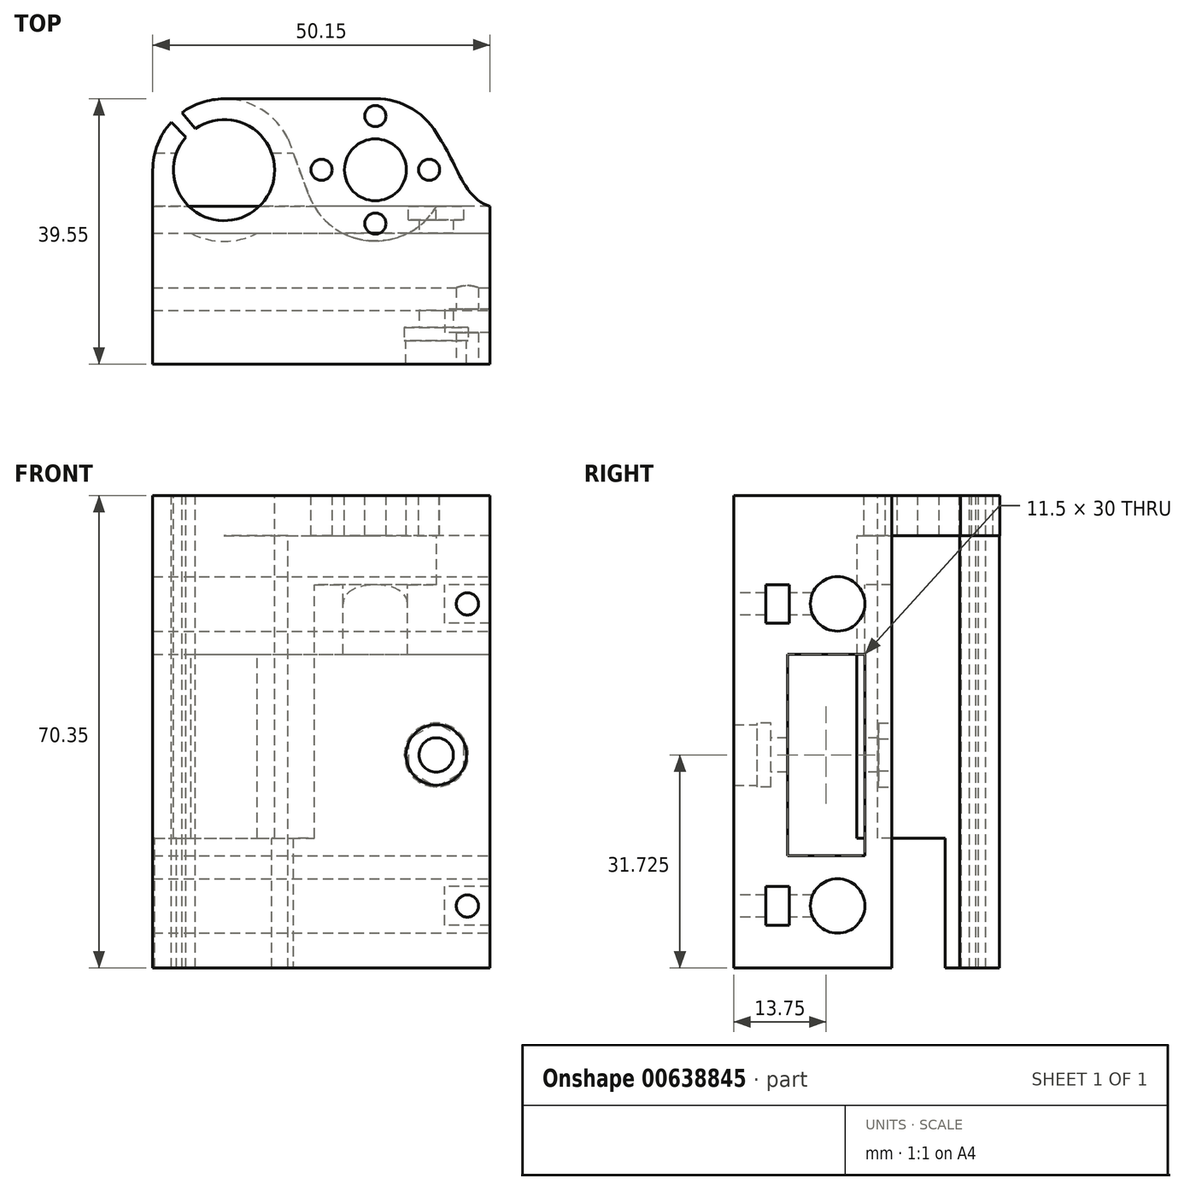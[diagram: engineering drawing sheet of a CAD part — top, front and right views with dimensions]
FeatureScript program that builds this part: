
annotation { "Feature Type Name" : "Feature", "Feature Type Description" : "" }
export const myFeature = defineFeature(function(context is Context, id is Id, definition is map)
    precondition{}
    {
        {
            var Q0;
            Q0=qCreatedBy(makeId("Top.planeOp"),FACE);
            var sketch = newSketch(context, id + "F0", { "sketchPlane" : qUnion([Q0])});
            skArc(sketch, "E0", {"start": v(-30.36, 19.22) * mm, "mid": v(-32.39, 15.91) * mm, "end": v(-33.1, 12.1) * mm});
            skCircle(sketch, "E1", {"center": v(0, 12.15) * mm, "radius": 10.6 * mm});
            skLineSegment(sketch, "E2", {"start": v(-33.1, 12.1) * mm, "end": v(-33.1, -13.3) * mm});
            skLineSegment(sketch, "E3", {"start": v(-33.1, -13.3) * mm, "end": v(17.05, -13.3) * mm});
            skLineSegment(sketch, "E4", {"start": v(17.05, -13.3) * mm, "end": v(17.05, 6.7) * mm});
            skArc(sketch, "E5", {"start": v(-28.18, 17.02) * mm, "mid": v(-17.48, 6.5) * mm, "end": v(-26.77, 18.29) * mm});
            skCircle(sketch, "E6", {"center": v(0, 12.15) * mm, "radius": 4.6 * mm});
            skLineSegment(sketch, "E7", {"start": v(-26.77, 18.29) * mm, "end": v(-28.78, 20.64) * mm});
            skLineSegment(sketch, "E8", {"start": v(-30.36, 19.22) * mm, "end": v(-28.18, 17.02) * mm});
            skArc(sketch, "E9.trimOffspring", {"start": v(-13, 16.8) * mm, "mid": v(-20, 22.4) * mm, "end": v(-28.78, 20.64) * mm});
            skCircle(sketch, "E10", {"center": v(0, 20.15) * mm, "radius": 1.57 * mm});
            skCircle(sketch, "E11", {"center": v(0, 4.15) * mm, "radius": 1.57 * mm});
            skCircle(sketch, "E12", {"center": v(8, 12.15) * mm, "radius": 1.57 * mm});
            skCircle(sketch, "E13", {"center": v(-8, 12.15) * mm, "radius": 1.57 * mm});
            skLineSegment(sketch, "E14", {"start": v(-13, 16.8) * mm, "end": v(-9.95, 8.5) * mm});
            skLineSegment(sketch, "E15", {"start": v(17.05, 6.7) * mm, "end": v(9.1, 6.7) * mm});
            skLineSegment(sketch, "E16", {"start": v(-22.52, 22.7) * mm, "end": v(0, 22.75) * mm});
            skFitSpline(sketch, "E17", {"points": [v(17.05, 6.7) * mm, v(9.47, 16.92) * mm], "startDerivative": vector(-12.18, 3.65) * mm, "endDerivative": vector(-7.6, 10.22) * mm});
            skCircle(sketch, "E18", {"center": v(-22.5, 12.1) * mm, "radius": 10.6 * mm});
            skSolve(sketch);
        }
        {
            var Q0;
            Q0=makeQuery(id+"F0.imprint","IMPRINT",FACE,{"disambiguationData":[TD([[makeQuery(id+"F0.imprint","IMPRINT",EDGE,{"derivedFrom":sQuery(id+"F0.wireOp",EDGE,"E0")}),1.0]])]});
            var Q1;
            {var subQ6=sQuery(id+"F0.wireOp",EDGE,"E2");Q1=makeQuery(id+"F0.imprint","IMPRINT",FACE,{"disambiguationData":[TD([[makeQuery(id+"F0.imprint","IMPRINT",EDGE,{"derivedFrom":subQ6}),1.0]])]});}
            extrude(context, id + "F1", {"entities" : qUnion([Q0, Q1]), "depth" : -70.35 * mm, "offsetDistance" : 25 * mm});
        }
        {
            var Q0;
            Q0=makeQuery(id+"F0.imprint","IMPRINT",FACE,{"disambiguationData":[TD([[makeQuery(id+"F0.imprint","IMPRINT",EDGE,{"derivedFrom":sQuery(id+"F0.wireOp",EDGE,"E6")}),-1.0]])]});
            var Q1;
            Q1 = qSketchRegion(id + "F3", true);
            var Q2;
            {var subQ0=sQuery(id+"F0.wireOp",EDGE,"E15");Q2=makeQuery(id+"F0.imprint","IMPRINT",FACE,{"disambiguationData":[TD([[makeQuery(id+"F0.imprint","IMPRINT",EDGE,{"derivedFrom":subQ0}),-1.0]])]});}
            var Q3;
            {var subQ0=sQuery(id+"F0.wireOp",EDGE,"E14");Q3=makeQuery(id+"F0.imprint","IMPRINT",FACE,{"disambiguationData":[TD([[makeQuery(id+"F0.imprint","IMPRINT",EDGE,{"derivedFrom":subQ0}),1.0]])]});}
            var Q4;
            {var subQ4=sQuery(id+"F0.wireOp",EDGE,"E16");Q4=makeQuery(id+"F0.imprint","IMPRINT",FACE,{"disambiguationData":[TD([[makeQuery(id+"F0.imprint","IMPRINT",EDGE,{"derivedFrom":subQ4}),-1.0]])]});}
            extrude(context, id + "F2", {"entities" : qUnion([Q0, Q1, Q2, Q3, Q4]), "operationType" : NewBodyOperationType.ADD, "depth" : -6 * mm, "offsetDistance" : 25 * mm});
        }
        {
            var Q0;
            Q0=qCreatedBy(makeId("Right.planeOp"),FACE);
            var sketch = newSketch(context, id + "F3", { "sketchPlane" : qUnion([Q0])});
            skCircle(sketch, "E19", {"center": v(-1.35, -16.15) * mm, "radius": 4.05 * mm});
            skCircle(sketch, "E20", {"center": v(-1.35, -61.1) * mm, "radius": 4.05 * mm});
            skLineSegment(sketch, "E21.bottom", {"start": v(2.7, -53.62) * mm, "end": v(-8.8, -53.62) * mm});
            skLineSegment(sketch, "E21.top", {"start": v(2.7, -23.62) * mm, "end": v(-8.8, -23.62) * mm});
            skLineSegment(sketch, "E21.left", {"start": v(2.7, -53.62) * mm, "end": v(2.7, -23.62) * mm});
            skLineSegment(sketch, "E21.right", {"start": v(-8.8, -53.62) * mm, "end": v(-8.8, -23.62) * mm});
            skPoint(sketch, "E21.middle", {"position": v(-3.05, -38.62) * mm});
            skSolve(sketch);
        }
        {
            var Q0;
            Q0=makeQuery(id+"F3.imprint","IMPRINT",FACE,{"disambiguationData":[TD([[makeQuery(id+"F3.imprint","IMPRINT",EDGE,{"derivedFrom":sQuery(id+"F3.wireOp",EDGE,"E19")}),1.0]])]});
            var Q1;
            Q1=makeQuery(id+"F3.imprint","IMPRINT",FACE,{"disambiguationData":[TD([[makeQuery(id+"F3.imprint","IMPRINT",EDGE,{"derivedFrom":sQuery(id+"F3.wireOp",EDGE,"E21.bottom")}),-1.0]])]});
            var Q2;
            Q2=makeQuery(id+"F3.imprint","IMPRINT",FACE,{"disambiguationData":[TD([[makeQuery(id+"F3.imprint","IMPRINT",EDGE,{"derivedFrom":sQuery(id+"F3.wireOp",EDGE,"E20")}),1.0]])]});
            extrude(context, id + "F4", {"entities" : qUnion([Q0, Q1, Q2]), "operationType" : NewBodyOperationType.REMOVE, "endBound" : BoundingType.THROUGH_ALL, "oppositeDirection" : true, "depth" : 25 * mm, "offsetDistance" : 25 * mm, "hasSecondDirection" : true, "secondDirectionOppositeDirection" : false, "secondDirectionDepth" : 50 * mm});
        }
        {
            var Q0;
            Q0=qCreatedBy(makeId("Right.planeOp"),FACE);
            cPlane(context, id + "F5", {"entities" : qUnion([Q0]), "cplaneType" : CPlaneType.OFFSET, "offset" : 10.3 * mm, "width" : 150 * mm, "height" : 150 * mm});
        }
        {
            var Q0;
            Q0=makeQuery(id+"F4.boolean.opBoolean","COPY",FACE,{"disambiguationData":[TD([makeQuery(id+"F1.opExtrude","SWEPT_FACE",FACE,{"disambiguationData":[OSD([sQuery(id+"F0.wireOp",EDGE,"E4")])]})])],"derivedFrom":makeQuery(id+"F4.opExtrude","SWEPT_FACE",FACE,{"disambiguationData":[OSD([sQuery(id+"F3.wireOp",EDGE,"E21.left")])]})});
            cPlane(context, id + "F6", {"entities" : qUnion([Q0]), "cplaneType" : CPlaneType.OFFSET, "offset" : 0 * mm, "width" : 150 * mm, "height" : 150 * mm});
        }
        {
            var Q0;
            Q0=qCreatedBy(id+"F6.planeOp",FACE);
            var sketch = newSketch(context, id + "F7", { "sketchPlane" : qUnion([Q0])});
            skLineSegment(sketch, "E22.bottom", {"start": v(9.1, -13.3) * mm, "end": v(-9.95, -13.3) * mm});
            skLineSegment(sketch, "E22.top", {"start": v(9.1, -53.62) * mm, "end": v(-9.95, -53.62) * mm});
            skLineSegment(sketch, "E22.left", {"start": v(9.1, -13.3) * mm, "end": v(9.1, -53.62) * mm});
            skLineSegment(sketch, "E22.right", {"start": v(-9.95, -13.3) * mm, "end": v(-9.95, -53.62) * mm});
            skSolve(sketch);
        }
        {
            var Q0;
            Q0 = qSketchRegion(id + "F7", true);
            extrude(context, id + "F8", {"entities" : qUnion([Q0]), "operationType" : NewBodyOperationType.ADD, "oppositeDirection" : true, "depth" : 4 * mm, "offsetDistance" : 25 * mm});
        }
        {
            var Q0;
            Q0=qCreatedBy(makeId("Right.planeOp"),FACE);
            var sketch = newSketch(context, id + "F9", { "sketchPlane" : qUnion([Q0])});
            skLineSegment(sketch, "E23", {"start": v(2.7, -50.17) * mm, "end": v(2.7, -70.35) * mm});
            skLineSegment(sketch, "E24", {"start": v(2.7, -70.35) * mm, "end": v(6.7, -70.35) * mm});
            skLineSegment(sketch, "E25", {"start": v(6.7, -70.35) * mm, "end": v(6.7, -50.17) * mm});
            skLineSegment(sketch, "E26", {"start": v(6.7, -50.17) * mm, "end": v(2.7, -50.17) * mm});
            skLineSegment(sketch, "E27", {"start": v(2.7, -21.1) * mm, "end": v(2.7, -23.62) * mm});
            skLineSegment(sketch, "E28", {"start": v(2.7, -23.62) * mm, "end": v(6.7, -23.62) * mm});
            skLineSegment(sketch, "E29", {"start": v(6.7, -23.62) * mm, "end": v(6.7, -21.1) * mm});
            skLineSegment(sketch, "E30", {"start": v(6.7, -21.1) * mm, "end": v(2.7, -21.1) * mm});
            skSolve(sketch);
        }
        {
            var Q0;
            Q0 = qSketchRegion(id + "F9", true);
            extrude(context, id + "F10", {"entities" : qUnion([Q0]), "operationType" : NewBodyOperationType.ADD, "endBound" : BoundingType.SYMMETRIC, "oppositeDirection" : true, "depth" : 10 * mm, "offsetDistance" : 25 * mm});
        }
        {
            var Q0;
            Q0=qCreatedBy(makeId("Front.planeOp"),FACE);
            var sketch = newSketch(context, id + "F11", { "sketchPlane" : qUnion([Q0])});
            skCircle(sketch, "E31", {"center": v(9.05, -38.62) * mm, "radius": 2.55 * mm});
            skSolve(sketch);
        }
        {
            var Q0;
            Q0 = qSketchRegion(id + "F11", true);
            extrude(context, id + "F12", {"entities" : qUnion([Q0]), "operationType" : NewBodyOperationType.REMOVE, "endBound" : BoundingType.SYMMETRIC, "oppositeDirection" : true, "depth" : 55 * mm, "offsetDistance" : 25 * mm});
        }
        {
            var Q0;
            Q0=makeQuery(id+"F8.opExtrude","CAP_FACE",FACE,{"disambiguationData":[OSD([sQuery(id+"F7.wireOp",EDGE,"E22.bottom"),sQuery(id+"F7.wireOp",EDGE,"E22.top"),sQuery(id+"F7.wireOp",EDGE,"E22.left"),sQuery(id+"F7.wireOp",EDGE,"E22.right")])],"isStart":false});
            cPlane(context, id + "F13", {"entities" : qUnion([Q0]), "cplaneType" : CPlaneType.OFFSET, "offset" : 0 * mm, "width" : 150 * mm, "height" : 150 * mm});
        }
        {
            var Q0;
            Q0=qCreatedBy(id+"F13.planeOp",FACE);
            var sketch = newSketch(context, id + "F14", { "sketchPlane" : qUnion([Q0])});
            skCircle(sketch, "E32.cCircle", {"center": v(-9.05, -38.63) * mm, "radius": 4.12 * mm, "construction": true});
            skLineSegment(sketch, "E32.0", {"start": v(-4.93, -41.01) * mm, "end": v(-9.06, -43.39) * mm});
            skLineSegment(sketch, "E32.1", {"start": v(-9.06, -43.39) * mm, "end": v(-13.18, -41) * mm});
            skLineSegment(sketch, "E32.2", {"start": v(-13.18, -41) * mm, "end": v(-13.17, -36.24) * mm});
            skLineSegment(sketch, "E32.3", {"start": v(-13.17, -36.24) * mm, "end": v(-9.04, -33.86) * mm});
            skLineSegment(sketch, "E32.4", {"start": v(-9.04, -33.86) * mm, "end": v(-4.92, -36.25) * mm});
            skLineSegment(sketch, "E32.5", {"start": v(-4.92, -36.25) * mm, "end": v(-4.93, -41.01) * mm});
            skPoint(sketch, "E32.0.midPoint", {"position": v(-7, -42.2) * mm});
            skSolve(sketch);
        }
        {
            var Q0;
            Q0 = qSketchRegion(id + "F14", true);
            extrude(context, id + "F15", {"entities" : qUnion([Q0]), "operationType" : NewBodyOperationType.REMOVE, "oppositeDirection" : true, "depth" : 2 * mm, "offsetDistance" : 25 * mm});
        }
        {
            var Q0;
            Q0=makeQuery(id+"F1.opExtrude","SWEPT_FACE",FACE,{"disambiguationData":[OSD([sQuery(id+"F0.wireOp",EDGE,"E3")])]});
            cPlane(context, id + "F16", {"entities" : qUnion([Q0]), "cplaneType" : CPlaneType.OFFSET, "offset" : 0 * mm, "width" : 150 * mm, "height" : 150 * mm});
        }
        {
            var Q0;
            Q0=qCreatedBy(id+"F16.planeOp",FACE);
            var sketch = newSketch(context, id + "F17", { "sketchPlane" : qUnion([Q0])});
            skCircle(sketch, "E33", {"center": v(9.05, -38.63) * mm, "radius": 4.75 * mm});
            skSolve(sketch);
        }
        {
            var Q0;
            Q0 = qSketchRegion(id + "F17", true);
            extrude(context, id + "F18", {"entities" : qUnion([Q0]), "operationType" : NewBodyOperationType.REMOVE, "oppositeDirection" : true, "depth" : 2 * mm, "offsetDistance" : 25 * mm});
        }
        {
            var Q0;
            Q0=makeQuery(id+"F0.imprint","IMPRINT",FACE,{"disambiguationData":[TD([[makeQuery(id+"F0.imprint","IMPRINT",EDGE,{"derivedFrom":sQuery(id+"F0.wireOp",EDGE,"E5")}),-1.0]])]});
            extrude(context, id + "F19", {"entities" : qUnion([Q0]), "oppositeDirection" : true, "depth" : 51 * mm, "offsetDistance" : 25 * mm});
        }
        {
            var Q0;
            Q0=qCreatedBy(makeId("Right.planeOp"),FACE);
            var sketch = newSketch(context, id + "F20", { "sketchPlane" : qUnion([Q0])});
            skLineSegment(sketch, "E34.bottom", {"start": v(14.66, -70.35) * mm, "end": v(6.7, -70.35) * mm});
            skLineSegment(sketch, "E34.top", {"start": v(14.66, -51) * mm, "end": v(6.7, -51) * mm});
            skLineSegment(sketch, "E34.left", {"start": v(14.66, -70.35) * mm, "end": v(14.66, -51) * mm});
            skLineSegment(sketch, "E34.right", {"start": v(6.7, -70.35) * mm, "end": v(6.7, -51) * mm});
            skSolve(sketch);
        }
        {
            var Q0;
            Q0 = qSketchRegion(id + "F20", true);
            extrude(context, id + "F21", {"entities" : qUnion([Q0]), "operationType" : NewBodyOperationType.REMOVE, "oppositeDirection" : true, "depth" : 35 * mm, "offsetDistance" : 25 * mm});
        }
        {
            var Q0;
            Q0=qCreatedBy(makeId("Right.planeOp"),FACE);
            var sketch = newSketch(context, id + "F22", { "sketchPlane" : qUnion([Q0])});
            skLineSegment(sketch, "E35.bottom", {"start": v(6.7, -51) * mm, "end": v(2.7, -51) * mm});
            skLineSegment(sketch, "E35.top", {"start": v(6.7, -70.35) * mm, "end": v(2.7, -70.35) * mm});
            skLineSegment(sketch, "E35.left", {"start": v(6.7, -51) * mm, "end": v(6.7, -70.35) * mm});
            skLineSegment(sketch, "E35.right", {"start": v(2.7, -51) * mm, "end": v(2.7, -70.35) * mm});
            skSolve(sketch);
        }
        {
            var Q0;
            Q0 = qSketchRegion(id + "F22", true);
            extrude(context, id + "F23", {"entities" : qUnion([Q0]), "operationType" : NewBodyOperationType.ADD, "oppositeDirection" : true, "depth" : 33 * mm, "offsetDistance" : 25 * mm});
        }
        {
            var Q0;
            Q0=qCreatedBy(id+"F5.planeOp",FACE);
            var sketch = newSketch(context, id + "F24", { "sketchPlane" : qUnion([Q0])});
            skLineSegment(sketch, "E36.bottom", {"start": v(-8.55, -19.02) * mm, "end": v(-12.05, -19.02) * mm});
            skLineSegment(sketch, "E36.top", {"start": v(-8.55, -13.27) * mm, "end": v(-12.05, -13.27) * mm});
            skLineSegment(sketch, "E36.left", {"start": v(-8.55, -19.02) * mm, "end": v(-8.55, -13.27) * mm});
            skLineSegment(sketch, "E36.right", {"start": v(-12.05, -19.02) * mm, "end": v(-12.05, -13.27) * mm});
            skPoint(sketch, "E36.middle", {"position": v(-10.3, -16.15) * mm});
            skLineSegment(sketch, "E37.bottom", {"start": v(-8.55, -63.98) * mm, "end": v(-12.05, -63.98) * mm});
            skLineSegment(sketch, "E37.top", {"start": v(-8.55, -58.23) * mm, "end": v(-12.05, -58.23) * mm});
            skLineSegment(sketch, "E37.left", {"start": v(-8.55, -63.98) * mm, "end": v(-8.55, -58.23) * mm});
            skLineSegment(sketch, "E37.right", {"start": v(-12.05, -63.98) * mm, "end": v(-12.05, -58.23) * mm});
            skPoint(sketch, "E37.middle", {"position": v(-10.3, -61.1) * mm});
            skSolve(sketch);
        }
        {
            var Q0;
            Q0 = qSketchRegion(id + "F24", true);
            extrude(context, id + "F25", {"entities" : qUnion([Q0]), "operationType" : NewBodyOperationType.REMOVE, "depth" : 25 * mm, "offsetDistance" : 25 * mm});
        }
        {
            var Q0;
            Q0=qCreatedBy(id+"F16.planeOp",FACE);
            var sketch = newSketch(context, id + "F26", { "sketchPlane" : qUnion([Q0])});
            skCircle(sketch, "E38", {"center": v(13.68, -16.15) * mm, "radius": 1.65 * mm});
            skCircle(sketch, "E39", {"center": v(13.68, -61.1) * mm, "radius": 1.65 * mm});
            skSolve(sketch);
        }
        {
            var Q0;
            Q0 = qSketchRegion(id + "F26", true);
            extrude(context, id + "F27", {"entities" : qUnion([Q0]), "operationType" : NewBodyOperationType.REMOVE, "oppositeDirection" : true, "depth" : 9 * mm, "offsetDistance" : 25 * mm});
        }
        {
            var Q0;
            Q0=qCreatedBy(id+"F16.planeOp",FACE);
            var sketch = newSketch(context, id + "F28", { "sketchPlane" : qUnion([Q0])});
            skLineSegment(sketch, "E40.bottom", {"start": v(-33.1, 0) * mm, "end": v(17.05, 0) * mm});
            skLineSegment(sketch, "E40.top", {"start": v(-33.1, -70.35) * mm, "end": v(17.05, -70.35) * mm});
            skLineSegment(sketch, "E40.left", {"start": v(-33.1, 0) * mm, "end": v(-33.1, -70.35) * mm});
            skLineSegment(sketch, "E40.right", {"start": v(17.05, 0) * mm, "end": v(17.05, -70.35) * mm});
            skCircle(sketch, "E41", {"center": v(9.05, -38.63) * mm, "radius": 4.5 * mm});
            skCircle(sketch, "E42", {"center": v(13.68, -16.15) * mm, "radius": 1.65 * mm});
            skCircle(sketch, "E43", {"center": v(13.68, -61.1) * mm, "radius": 1.65 * mm});
            skSolve(sketch);
        }
        {
            var Q0;
            Q0 = qSketchRegion(id + "F28", true);
            extrude(context, id + "F29", {"entities" : qUnion([Q0]), "operationType" : NewBodyOperationType.ADD, "depth" : 3.5 * mm, "offsetDistance" : 25 * mm});
        }
        {
            var Q0;
            Q0=qCreatedBy(id+"F13.planeOp",FACE);
            var sketch = newSketch(context, id + "F30", { "sketchPlane" : qUnion([Q0])});
            skLineSegment(sketch, "E44.bottom", {"start": v(-17.05, -53.62) * mm, "end": v(33.1, -53.62) * mm});
            skLineSegment(sketch, "E44.top", {"start": v(-17.05, -70.35) * mm, "end": v(33.1, -70.35) * mm});
            skLineSegment(sketch, "E44.left", {"start": v(-17.05, -53.62) * mm, "end": v(-17.05, -70.35) * mm});
            skLineSegment(sketch, "E44.right", {"start": v(33.1, -53.62) * mm, "end": v(33.1, -70.35) * mm});
            skSolve(sketch);
        }
        {
            var Q0;
            Q0 = qSketchRegion(id + "F30", true);
            extrude(context, id + "F31", {"entities" : qUnion([Q0]), "operationType" : NewBodyOperationType.ADD, "oppositeDirection" : true, "depth" : 6 * mm, "offsetDistance" : 25 * mm});
        }
        {
            var Q0;
            Q0=qCreatedBy(id+"F5.planeOp",FACE);
            var sketch = newSketch(context, id + "F32", { "sketchPlane" : qUnion([Q0])});
            skCircle(sketch, "E45", {"center": v(-1.35, -61.1) * mm, "radius": 4.05 * mm});
            skCircle(sketch, "E46", {"center": v(-1.35, -16.15) * mm, "radius": 4.05 * mm});
            skSolve(sketch);
        }
        {
            var Q0;
            Q0 = qSketchRegion(id + "F32", true);
            extrude(context, id + "F33", {"entities" : qUnion([Q0]), "operationType" : NewBodyOperationType.REMOVE, "endBound" : BoundingType.SYMMETRIC, "oppositeDirection" : true, "depth" : 150 * mm, "offsetDistance" : 25 * mm});
        }
    });
